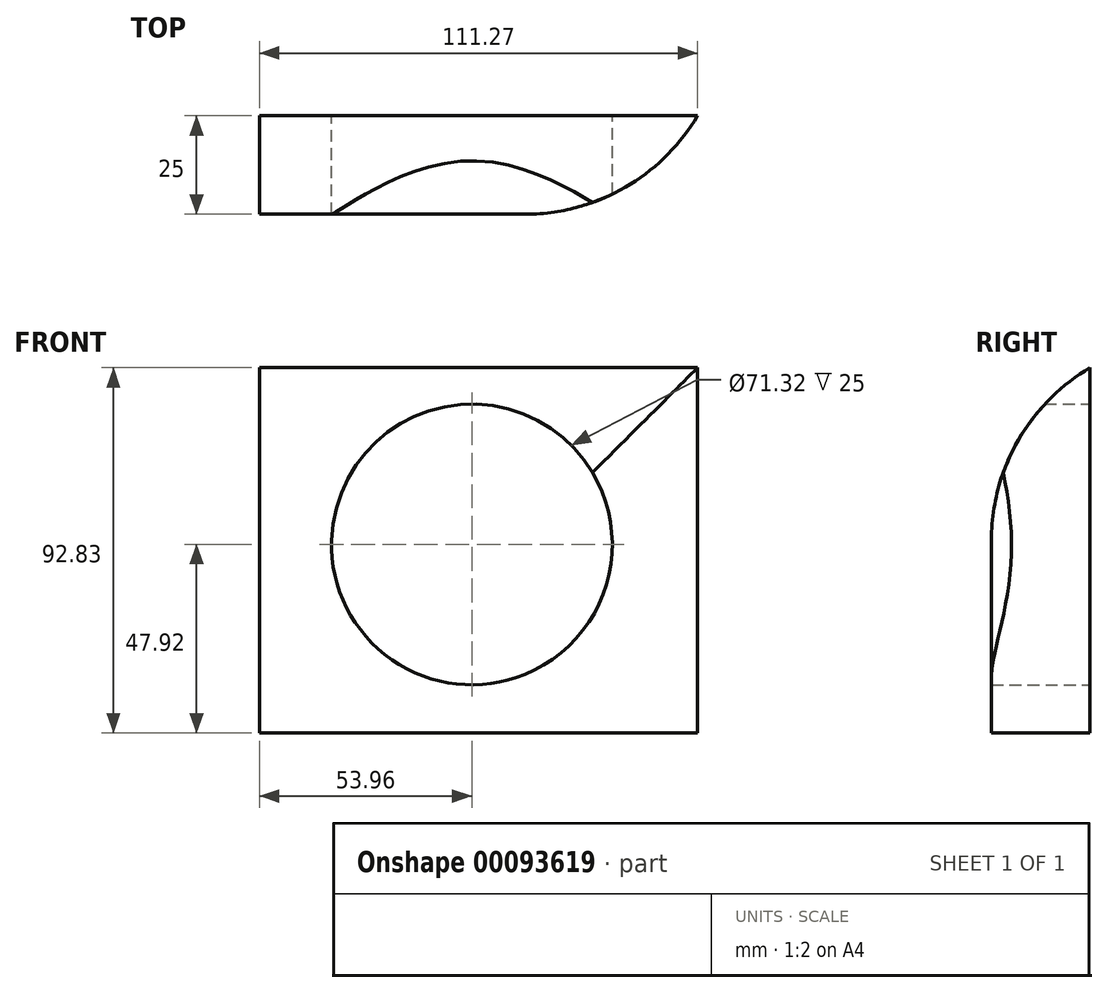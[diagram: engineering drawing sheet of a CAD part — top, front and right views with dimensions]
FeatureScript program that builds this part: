
annotation { "Feature Type Name" : "Feature", "Feature Type Description" : "" }
export const myFeature = defineFeature(function(context is Context, id is Id, definition is map)
    precondition{}
    {
        {
            var Q0;
            Q0=qCreatedBy(makeId("Front.planeOp"),FACE);
            var sketch = newSketch(context, id + "F0", { "sketchPlane" : qUnion([Q0])});
            skLineSegment(sketch, "E0.bottom", {"start": v(-53.96, 44.9) * mm, "end": v(57.3, 44.9) * mm});
            skLineSegment(sketch, "E0.top", {"start": v(-53.96, -47.92) * mm, "end": v(57.3, -47.92) * mm});
            skLineSegment(sketch, "E0.left", {"start": v(-53.96, 44.9) * mm, "end": v(-53.96, -47.92) * mm});
            skLineSegment(sketch, "E0.right", {"start": v(57.3, 44.9) * mm, "end": v(57.3, -47.92) * mm});
            skCircle(sketch, "E1", {"center": v(0, 0) * mm, "radius": 35.66 * mm});
            skSolve(sketch);
        }
        {
            var Q0;
            Q0=makeQuery(id+"F0.imprint","IMPRINT",FACE,{"disambiguationData":[TD([[makeQuery(id+"F0.imprint","IMPRINT",EDGE,{"derivedFrom":sQuery(id+"F0.wireOp",EDGE,"E0.bottom")}),-1.0]])]});
            extrude(context, id + "F1", {"entities" : qUnion([Q0]), "depth" : 25 * mm});
        }
        {
            var Q0;
            Q0=makeQuery(id+"F1.opExtrude","CAP_EDGE",EDGE,{"disambiguationData":[OSD([sQuery(id+"F0.wireOp",EDGE,"E0.right")])],"isStart":false});
            var Q1;
            Q1=makeQuery(id+"F1.opExtrude","CAP_EDGE",EDGE,{"disambiguationData":[OSD([sQuery(id+"F0.wireOp",EDGE,"E0.bottom")])],"isStart":false});
            fillet(context, id + "F2", {"entities" : qUnion([Q0, Q1]), "radius" : 51 * mm, "allowEdgeOverflow" : false});
        }
    });
